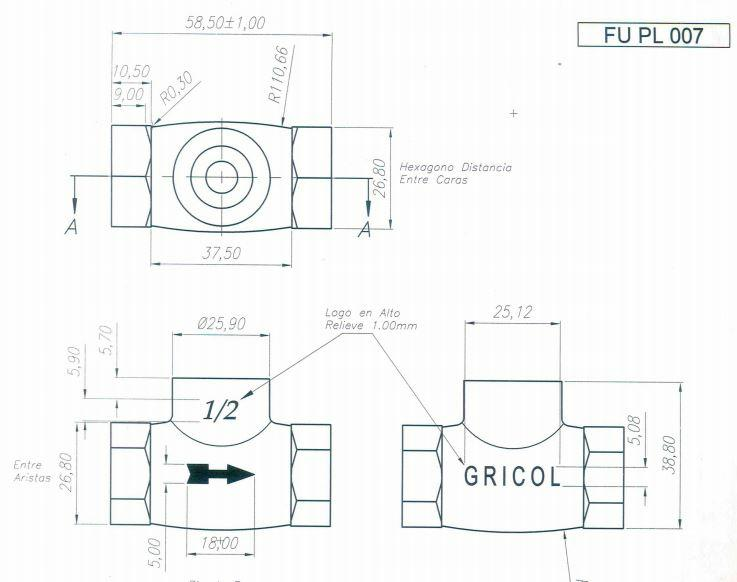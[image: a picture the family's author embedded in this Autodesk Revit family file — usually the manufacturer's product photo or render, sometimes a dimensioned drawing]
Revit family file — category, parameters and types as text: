
# Revit family: 01-1901-15 LLAVE MANGUERA PLASTICA BLANCA
name_source: partatom
category: Aparatos sanitarios
units: mm (PartAtom-declared; Revit-internal decimal feet)

## family parameters
Anfitrión = Cara
Compartido = No
Corte con vacíos al cargar = No
Cota de conector redondo = Diámetro de uso
Número OmniClass = 23.31.11.00
Punto de cálculo de habitación = No
Tipo de pieza = Normal

## types (1)
- 01-1901-15
    Acometida = Dim 1/2" NPT
    Ancho = 106.3 mm  [stored 0.348753 ft]
    Ancho manija llave = 60 mm
    Conexión AC = Sí
    Conexión AF = Sí
    Conexión de residuos = No
    Conexión de ventilación = No
    Descripción = Llave jardin
    Elevación por defecto = 0 mm  [stored 0 ft]
    Fabricante = Gricol
    Imagen de tipo = LLAVE MANGUERA PLASTICA BLANCA.JPG
    Link Ficha Tecnica = http://infotecnica.gricol.com
    Modelo = 01-1901-15
    Plastico - ABS + Colorante blanco = Plastico - ABS + Colorante blanco
    Product Name = LLAVE MANGUERA PLASTICA BLANCA
    Salida = Dim 3/4" NH
    URL = https://www.gricol.com

note: [stored X ft] marks values corroborated as IEEE doubles in the binary element streams (Revit-internal decimal feet)

## geometry (parser evidence)
native form markers: Blend x4, Sweep x4
no freeform markers — native parametric forms only
